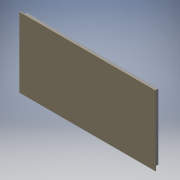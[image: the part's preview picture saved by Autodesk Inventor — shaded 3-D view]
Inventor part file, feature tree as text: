
AUTODESK INVENTOR PART (.ipt)
format: ipt  version: 2019 (Build 230136000, 136)  size: 99,840 bytes
history: native  units: mm
features: other x6, reference x4, extrude x2, sketch x2
ambient origin geometry x8: Origin, YZ Plane, XZ Plane, XY Plane, X Axis, Y Axis, Z Axis, Center Point
bodies: Solid1 (feature_tree)
feature tree (14):
  extrude  "Extrusion1"  Depth=774.7mm
  extrude  "Extrusion2"  Depth=25.4mm TaperAngle=0.0deg
  sketch  "Sketch1"  dims[d0=4.7625mm d1=0.0mm d2=774.7mm]
  sketch  "Sketch2"  dims[d3=398.78mm d4=25.4mm d5=0.0mm]
  reference  "Reference1"
  reference  "Reference2"
  reference  "Reference3"
  reference  "Reference4"
  parser-record x1  (decoder bookkeeping rows leaked as tree rows — omitted from the tree; the rows remain in map.json)
  other  "front_door.iam"
  other  "1515-S-BLACK_front_door_cross:2"
  other  "1515-S-BLACK_front_door_side:2"
  other  "1515-S-BLACK_front_door_cross:1"
  other  "1515-S-BLACK_front_door_side:1"
note: 1 file-system path scrubbed to <path> (originals preserved in map.json)
